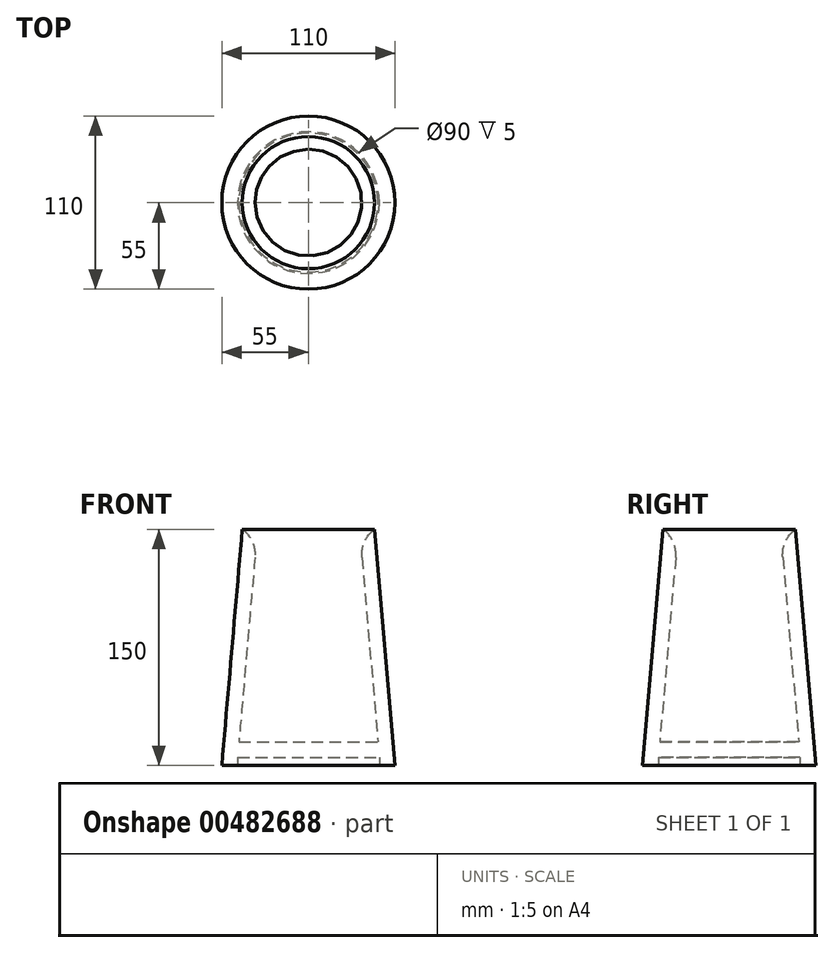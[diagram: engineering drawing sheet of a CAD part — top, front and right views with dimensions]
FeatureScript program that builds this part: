
annotation { "Feature Type Name" : "Feature", "Feature Type Description" : "" }
export const myFeature = defineFeature(function(context is Context, id is Id, definition is map)
    precondition{}
    {
        {
            var Q0;
            Q0=qCreatedBy(makeId("Front.planeOp"),FACE);
            var sketch = newSketch(context, id + "F0", { "sketchPlane" : qUnion([Q0])});
            skLineSegment(sketch, "E0", {"start": v(0, 5) * mm, "end": v(-45, 5) * mm});
            skLineSegment(sketch, "E1", {"start": v(-45, 5) * mm, "end": v(-45, 0) * mm});
            skLineSegment(sketch, "E2", {"start": v(0, 0) * mm, "end": v(0, 150) * mm, "construction": true});
            skLineSegment(sketch, "E3", {"start": v(-45, 0) * mm, "end": v(-55, 0) * mm});
            skLineSegment(sketch, "E4", {"start": v(-55, 0) * mm, "end": v(-42, 150) * mm});
            skLineSegment(sketch, "E5", {"start": v(-45, 5) * mm, "end": v(-32.42, 150.18) * mm});
            skLineSegment(sketch, "E6", {"start": v(-42, 150) * mm, "end": v(-32.42, 150.18) * mm});
            skLineSegment(sketch, "E7", {"start": v(0, 150) * mm, "end": v(-42, 150) * mm, "construction": true});
            skLineSegment(sketch, "E8", {"start": v(0, 5) * mm, "end": v(0, 15) * mm});
            skLineSegment(sketch, "E9", {"start": v(0, 15) * mm, "end": v(-44.13, 15) * mm});
            skSolve(sketch);
        }
        {
            var Q0;
            {var subQ1=sQuery(id+"F0.wireOp",EDGE,"E1");Q0=makeQuery(id+"F0.imprint","IMPRINT",FACE,{"disambiguationData":[TD([[makeQuery(id+"F0.imprint","IMPRINT",EDGE,{"derivedFrom":subQ1}),-1.0]])]});}
            var Q1;
            {var subQ0=sQuery(id+"F0.wireOp",EDGE,"E0");Q1=makeQuery(id+"F0.imprint","IMPRINT",FACE,{"disambiguationData":[TD([[makeQuery(id+"F0.imprint","IMPRINT",EDGE,{"derivedFrom":subQ0}),-1.0]])]});}
            var Q2;
            Q2=sQuery(id+"F0.wireOp",EDGE,"E2");
            revolve(context, id + "F1", {"entities" : qUnion([Q0, Q1]), "axis" : qUnion([Q2]), "revolveType" : RevolveType.FULL});
        }
        {
            var Q0;
            Q0=makeQuery(id+"F1.opRevolve","SWEPT_EDGE",EDGE,{"disambiguationData":[OSD([sQuery(id+"F0.wireOp",EDGE,"E5"),sQuery(id+"F0.wireOp",EDGE,"E6")])]});
            fillet(context, id + "F2", {"entities" : qUnion([Q0]), "radius" : 20 * mm, "tangentPropagation" : true, "allowEdgeOverflow" : false});
        }
    });
